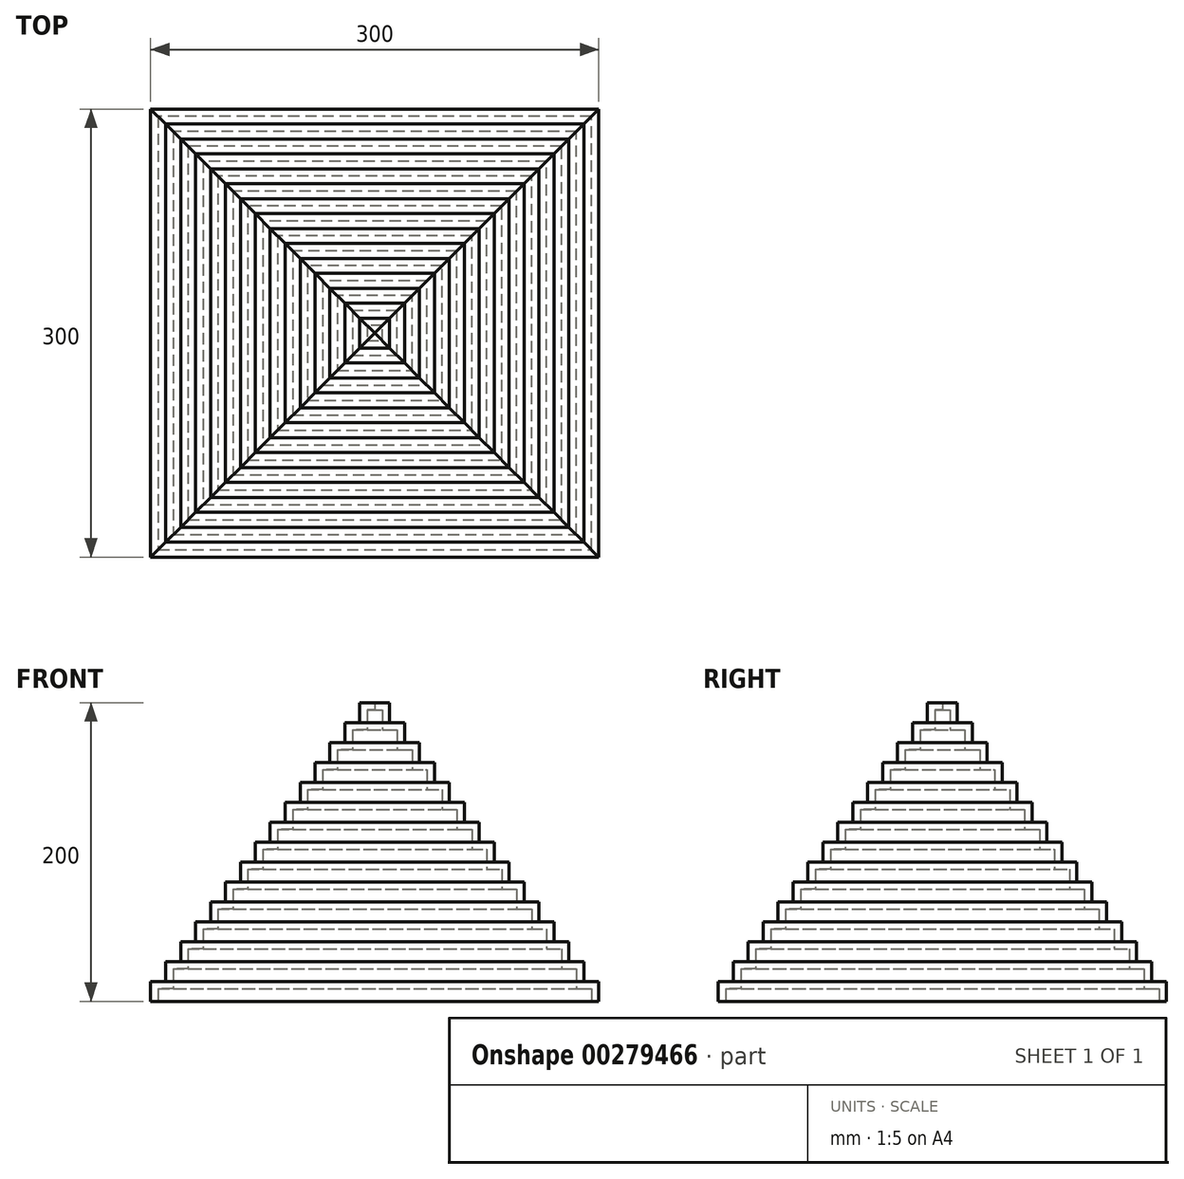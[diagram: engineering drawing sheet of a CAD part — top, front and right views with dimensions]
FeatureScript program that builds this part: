
annotation { "Feature Type Name" : "Feature", "Feature Type Description" : "" }
export const myFeature = defineFeature(function(context is Context, id is Id, definition is map)
    precondition{}
    {
        {
            var Q0;
            Q0=qCreatedBy(makeId("Front.planeOp"),FACE);
            var sketch = newSketch(context, id + "F0", { "sketchPlane" : qUnion([Q0])});
            skLineSegment(sketch, "E0", {"start": v(-150, 0) * mm, "end": v(150, 0) * mm, "construction": true});
            skLineSegment(sketch, "E1", {"start": v(150, 0) * mm, "end": v(150, 13.33) * mm});
            skLineSegment(sketch, "E2", {"start": v(150, 13.33) * mm, "end": v(140, 13.33) * mm});
            skLineSegment(sketch, "E3", {"start": v(140, 13.33) * mm, "end": v(140, 26.67) * mm});
            skLineSegment(sketch, "E4", {"start": v(140, 26.67) * mm, "end": v(130, 26.67) * mm});
            skLineSegment(sketch, "E5", {"start": v(130, 26.67) * mm, "end": v(130, 40) * mm});
            skLineSegment(sketch, "E6", {"start": v(130, 40) * mm, "end": v(120, 40) * mm});
            skLineSegment(sketch, "E7", {"start": v(120, 40) * mm, "end": v(120, 53.33) * mm});
            skLineSegment(sketch, "E8", {"start": v(120, 53.33) * mm, "end": v(110, 53.33) * mm});
            skLineSegment(sketch, "E9", {"start": v(110, 53.33) * mm, "end": v(110, 66.67) * mm});
            skLineSegment(sketch, "E10", {"start": v(110, 66.67) * mm, "end": v(100, 66.67) * mm});
            skLineSegment(sketch, "E11", {"start": v(100, 66.67) * mm, "end": v(100, 80) * mm});
            skLineSegment(sketch, "E12", {"start": v(100, 80) * mm, "end": v(90, 80) * mm});
            skLineSegment(sketch, "E13", {"start": v(90, 80) * mm, "end": v(90, 93.33) * mm});
            skLineSegment(sketch, "E14", {"start": v(90, 93.33) * mm, "end": v(80, 93.33) * mm});
            skLineSegment(sketch, "E15", {"start": v(80, 93.33) * mm, "end": v(80, 106.67) * mm});
            skLineSegment(sketch, "E16", {"start": v(80, 106.67) * mm, "end": v(70, 106.67) * mm});
            skLineSegment(sketch, "E17", {"start": v(70, 106.67) * mm, "end": v(70, 120) * mm});
            skLineSegment(sketch, "E18", {"start": v(70, 120) * mm, "end": v(60, 120) * mm});
            skLineSegment(sketch, "E19", {"start": v(60, 120) * mm, "end": v(60, 133.33) * mm});
            skLineSegment(sketch, "E20", {"start": v(60, 133.33) * mm, "end": v(50, 133.33) * mm});
            skLineSegment(sketch, "E21", {"start": v(50, 133.33) * mm, "end": v(50, 146.67) * mm});
            skLineSegment(sketch, "E22", {"start": v(50, 146.67) * mm, "end": v(40, 146.67) * mm});
            skLineSegment(sketch, "E23", {"start": v(40, 146.67) * mm, "end": v(40, 160) * mm});
            skLineSegment(sketch, "E24", {"start": v(40, 160) * mm, "end": v(30, 160) * mm});
            skLineSegment(sketch, "E25", {"start": v(30, 160) * mm, "end": v(30, 173.33) * mm});
            skLineSegment(sketch, "E26", {"start": v(30, 173.33) * mm, "end": v(20, 173.33) * mm});
            skLineSegment(sketch, "E27", {"start": v(20, 173.33) * mm, "end": v(20, 186.67) * mm});
            skLineSegment(sketch, "E28", {"start": v(20, 186.67) * mm, "end": v(10, 186.67) * mm});
            skLineSegment(sketch, "E29", {"start": v(10, 186.67) * mm, "end": v(10, 200) * mm});
            skLineSegment(sketch, "E30", {"start": v(10, 200) * mm, "end": v(0, 200) * mm});
            skLineSegment(sketch, "E31", {"start": v(0, 0) * mm, "end": v(0, 87.04) * mm, "construction": true});
            skLineSegment(sketch, "E32.0", {"start": v(5, 195) * mm, "end": v(0, 195) * mm});
            skLineSegment(sketch, "E32.1", {"start": v(5, 181.67) * mm, "end": v(5, 195) * mm});
            skLineSegment(sketch, "E32.2", {"start": v(15, 181.67) * mm, "end": v(5, 181.67) * mm});
            skLineSegment(sketch, "E32.3", {"start": v(15, 168.33) * mm, "end": v(15, 181.67) * mm});
            skLineSegment(sketch, "E32.4", {"start": v(25, 168.33) * mm, "end": v(15, 168.33) * mm});
            skLineSegment(sketch, "E32.5", {"start": v(25, 155) * mm, "end": v(25, 168.33) * mm});
            skLineSegment(sketch, "E32.6", {"start": v(35, 155) * mm, "end": v(25, 155) * mm});
            skLineSegment(sketch, "E32.7", {"start": v(35, 141.67) * mm, "end": v(35, 155) * mm});
            skLineSegment(sketch, "E32.8", {"start": v(105, 61.67) * mm, "end": v(95, 61.67) * mm});
            skLineSegment(sketch, "E32.9", {"start": v(105, 48.33) * mm, "end": v(105, 61.67) * mm});
            skLineSegment(sketch, "E32.10", {"start": v(115, 48.33) * mm, "end": v(105, 48.33) * mm});
            skLineSegment(sketch, "E32.11", {"start": v(115, 35) * mm, "end": v(115, 48.33) * mm});
            skLineSegment(sketch, "E32.12", {"start": v(125, 35) * mm, "end": v(115, 35) * mm});
            skLineSegment(sketch, "E32.13", {"start": v(125, 21.67) * mm, "end": v(125, 35) * mm});
            skLineSegment(sketch, "E32.14", {"start": v(145, 0) * mm, "end": v(145, 8.33) * mm});
            skLineSegment(sketch, "E32.15", {"start": v(145, 8.33) * mm, "end": v(135, 8.33) * mm});
            skLineSegment(sketch, "E32.16", {"start": v(135, 8.33) * mm, "end": v(135, 21.67) * mm});
            skLineSegment(sketch, "E32.17", {"start": v(135, 21.67) * mm, "end": v(125, 21.67) * mm});
            skLineSegment(sketch, "E32.18", {"start": v(95, 61.67) * mm, "end": v(95, 75) * mm});
            skLineSegment(sketch, "E32.19", {"start": v(95, 75) * mm, "end": v(85, 75) * mm});
            skLineSegment(sketch, "E32.20", {"start": v(85, 75) * mm, "end": v(85, 88.33) * mm});
            skLineSegment(sketch, "E32.21", {"start": v(85, 88.33) * mm, "end": v(75, 88.33) * mm});
            skLineSegment(sketch, "E32.22", {"start": v(75, 88.33) * mm, "end": v(75, 101.67) * mm});
            skLineSegment(sketch, "E32.23", {"start": v(75, 101.67) * mm, "end": v(65, 101.67) * mm});
            skLineSegment(sketch, "E32.24", {"start": v(65, 101.67) * mm, "end": v(65, 115) * mm});
            skLineSegment(sketch, "E32.25", {"start": v(65, 115) * mm, "end": v(55, 115) * mm});
            skLineSegment(sketch, "E32.26", {"start": v(55, 115) * mm, "end": v(55, 128.33) * mm});
            skLineSegment(sketch, "E32.27", {"start": v(55, 128.33) * mm, "end": v(45, 128.33) * mm});
            skLineSegment(sketch, "E32.28", {"start": v(45, 128.33) * mm, "end": v(45, 141.67) * mm});
            skLineSegment(sketch, "E32.29", {"start": v(45, 141.67) * mm, "end": v(35, 141.67) * mm});
            skLineSegment(sketch, "E33", {"start": v(145, 0) * mm, "end": v(150, 0) * mm});
            skLineSegment(sketch, "E34", {"start": v(0, 200) * mm, "end": v(0, 195) * mm});
            skSolve(sketch);
        }
        {
            var Q0;
            Q0 = qSketchRegion(id + "F0", true);
            extrude(context, id + "F1", {"entities" : qUnion([Q0]), "depth" : 150 * mm, "hasSecondDirection" : true, "secondDirectionOppositeDirection" : true, "secondDirectionDepth" : 150 * mm});
        }
        {
            var Q0;
            Q0=qCreatedBy(makeId("Right.planeOp"),FACE);
            var sketch = newSketch(context, id + "F2", { "sketchPlane" : qUnion([Q0])});
            skLineSegment(sketch, "E35", {"start": v(-150, 0) * mm, "end": v(150, 0) * mm, "construction": true});
            skLineSegment(sketch, "E36", {"start": v(0, 0) * mm, "end": v(0, 200) * mm});
            skLineSegment(sketch, "E37", {"start": v(150, 0) * mm, "end": v(150, 13.33) * mm});
            skSolve(sketch);
        }
        {
            var Q0;
            Q0=qCreatedBy(makeId("Right.planeOp"),FACE);
            var Q1;
            Q1=sQuery(id+"F2.wireOp",EDGE,"E36");
            cPlane(context, id + "F3", {"entities" : qUnion([Q0, Q1]), "cplaneType" : CPlaneType.LINE_ANGLE, "offset" : 47 * mm, "angle" : 45 * degree, "oppositeDirection" : true, "width" : 150 * mm, "height" : 150 * mm});
        }
        {
            var Q0;
            Q0=qCreatedBy(id+"F3.planeOp",FACE);
            var sketch = newSketch(context, id + "F4", { "sketchPlane" : qUnion([Q0])});
            skLineSegment(sketch, "E38.bottom", {"start": v(136.08, 226.9) * mm, "end": v(0, 226.9) * mm});
            skLineSegment(sketch, "E38.top", {"start": v(136.08, -11.6) * mm, "end": v(0, -11.6) * mm});
            skLineSegment(sketch, "E38.left", {"start": v(136.08, 226.9) * mm, "end": v(136.08, -11.6) * mm});
            skLineSegment(sketch, "E38.right", {"start": v(0, 226.9) * mm, "end": v(0, -11.6) * mm});
            skSolve(sketch);
        }
        {
            var Q0;
            Q0 = qSketchRegion(id + "F4", true);
            extrude(context, id + "F5", {"entities" : qUnion([Q0]), "operationType" : NewBodyOperationType.REMOVE, "endBound" : BoundingType.THROUGH_ALL, "oppositeDirection" : true, "depth" : 25 * mm});
        }
        {
            var Q0;
            Q0=qCreatedBy(makeId("Right.planeOp"),FACE);
            var Q1;
            Q1=sQuery(id+"F2.wireOp",EDGE,"E36");
            cPlane(context, id + "F6", {"entities" : qUnion([Q0, Q1]), "cplaneType" : CPlaneType.LINE_ANGLE, "offset" : 25 * mm, "angle" : 45 * degree, "width" : 150 * mm, "height" : 150 * mm});
        }
        {
            var Q0;
            Q0=qCreatedBy(id+"F6.planeOp",FACE);
            var sketch = newSketch(context, id + "F7", { "sketchPlane" : qUnion([Q0])});
            skLineSegment(sketch, "E39.bottom", {"start": v(-211.06, 218.4) * mm, "end": v(0, 218.4) * mm});
            skLineSegment(sketch, "E39.top", {"start": v(-211.06, -13.72) * mm, "end": v(0, -13.72) * mm});
            skLineSegment(sketch, "E39.left", {"start": v(-211.06, 218.4) * mm, "end": v(-211.06, -13.72) * mm});
            skLineSegment(sketch, "E39.right", {"start": v(0, 218.4) * mm, "end": v(0, -13.72) * mm});
            skSolve(sketch);
        }
        {
            var Q0;
            Q0 = qSketchRegion(id + "F7", true);
            extrude(context, id + "F8", {"entities" : qUnion([Q0]), "operationType" : NewBodyOperationType.REMOVE, "endBound" : BoundingType.THROUGH_ALL, "oppositeDirection" : true, "depth" : 25 * mm});
        }
        {
            var Q0;
            Q0=makeQuery(id+"F1.opExtrude","SWEPT_BODY",BODY,{"disambiguationData":[OSD([sQuery(id+"F0.wireOp",EDGE,"E1"),sQuery(id+"F0.wireOp",EDGE,"E2"),sQuery(id+"F0.wireOp",EDGE,"E3"),sQuery(id+"F0.wireOp",EDGE,"E4"),sQuery(id+"F0.wireOp",EDGE,"E5"),sQuery(id+"F0.wireOp",EDGE,"E6"),sQuery(id+"F0.wireOp",EDGE,"E7"),sQuery(id+"F0.wireOp",EDGE,"E8"),sQuery(id+"F0.wireOp",EDGE,"E9"),sQuery(id+"F0.wireOp",EDGE,"E10"),sQuery(id+"F0.wireOp",EDGE,"E11"),sQuery(id+"F0.wireOp",EDGE,"E12"),sQuery(id+"F0.wireOp",EDGE,"E13"),sQuery(id+"F0.wireOp",EDGE,"E14"),sQuery(id+"F0.wireOp",EDGE,"E15"),sQuery(id+"F0.wireOp",EDGE,"E16"),sQuery(id+"F0.wireOp",EDGE,"E17"),sQuery(id+"F0.wireOp",EDGE,"E18"),sQuery(id+"F0.wireOp",EDGE,"E19"),sQuery(id+"F0.wireOp",EDGE,"E20"),sQuery(id+"F0.wireOp",EDGE,"E21"),sQuery(id+"F0.wireOp",EDGE,"E22"),sQuery(id+"F0.wireOp",EDGE,"E23"),sQuery(id+"F0.wireOp",EDGE,"E24"),sQuery(id+"F0.wireOp",EDGE,"E25"),sQuery(id+"F0.wireOp",EDGE,"E26"),sQuery(id+"F0.wireOp",EDGE,"E27"),sQuery(id+"F0.wireOp",EDGE,"E28"),sQuery(id+"F0.wireOp",EDGE,"E29"),sQuery(id+"F0.wireOp",EDGE,"E30"),sQuery(id+"F0.wireOp",EDGE,"E32.0"),sQuery(id+"F0.wireOp",EDGE,"E32.1"),sQuery(id+"F0.wireOp",EDGE,"E32.2"),sQuery(id+"F0.wireOp",EDGE,"E32.3"),sQuery(id+"F0.wireOp",EDGE,"E32.4"),sQuery(id+"F0.wireOp",EDGE,"E32.5"),sQuery(id+"F0.wireOp",EDGE,"E32.6"),sQuery(id+"F0.wireOp",EDGE,"E32.7"),sQuery(id+"F0.wireOp",EDGE,"E32.8"),sQuery(id+"F0.wireOp",EDGE,"E32.9"),sQuery(id+"F0.wireOp",EDGE,"E32.10"),sQuery(id+"F0.wireOp",EDGE,"E32.11"),sQuery(id+"F0.wireOp",EDGE,"E32.12"),sQuery(id+"F0.wireOp",EDGE,"E32.13"),sQuery(id+"F0.wireOp",EDGE,"E32.14"),sQuery(id+"F0.wireOp",EDGE,"E32.15"),sQuery(id+"F0.wireOp",EDGE,"E32.16"),sQuery(id+"F0.wireOp",EDGE,"E32.17"),sQuery(id+"F0.wireOp",EDGE,"E32.18"),sQuery(id+"F0.wireOp",EDGE,"E32.19"),sQuery(id+"F0.wireOp",EDGE,"E32.20"),sQuery(id+"F0.wireOp",EDGE,"E32.21"),sQuery(id+"F0.wireOp",EDGE,"E32.22"),sQuery(id+"F0.wireOp",EDGE,"E32.23"),sQuery(id+"F0.wireOp",EDGE,"E32.24"),sQuery(id+"F0.wireOp",EDGE,"E32.25"),sQuery(id+"F0.wireOp",EDGE,"E32.26"),sQuery(id+"F0.wireOp",EDGE,"E32.27"),sQuery(id+"F0.wireOp",EDGE,"E32.28"),sQuery(id+"F0.wireOp",EDGE,"E32.29"),sQuery(id+"F0.wireOp",EDGE,"E33"),sQuery(id+"F0.wireOp",EDGE,"E34")])]});
            var Q1;
            Q1=sQuery(id+"F2.wireOp",EDGE,"E36");
            circularPattern(context, id + "F9", {"entities" : qUnion([Q0]), "axis" : qUnion([Q1]), "angle" : 360 * degree, "instanceCount" : 4, "equalSpace" : true});
        }
    });
